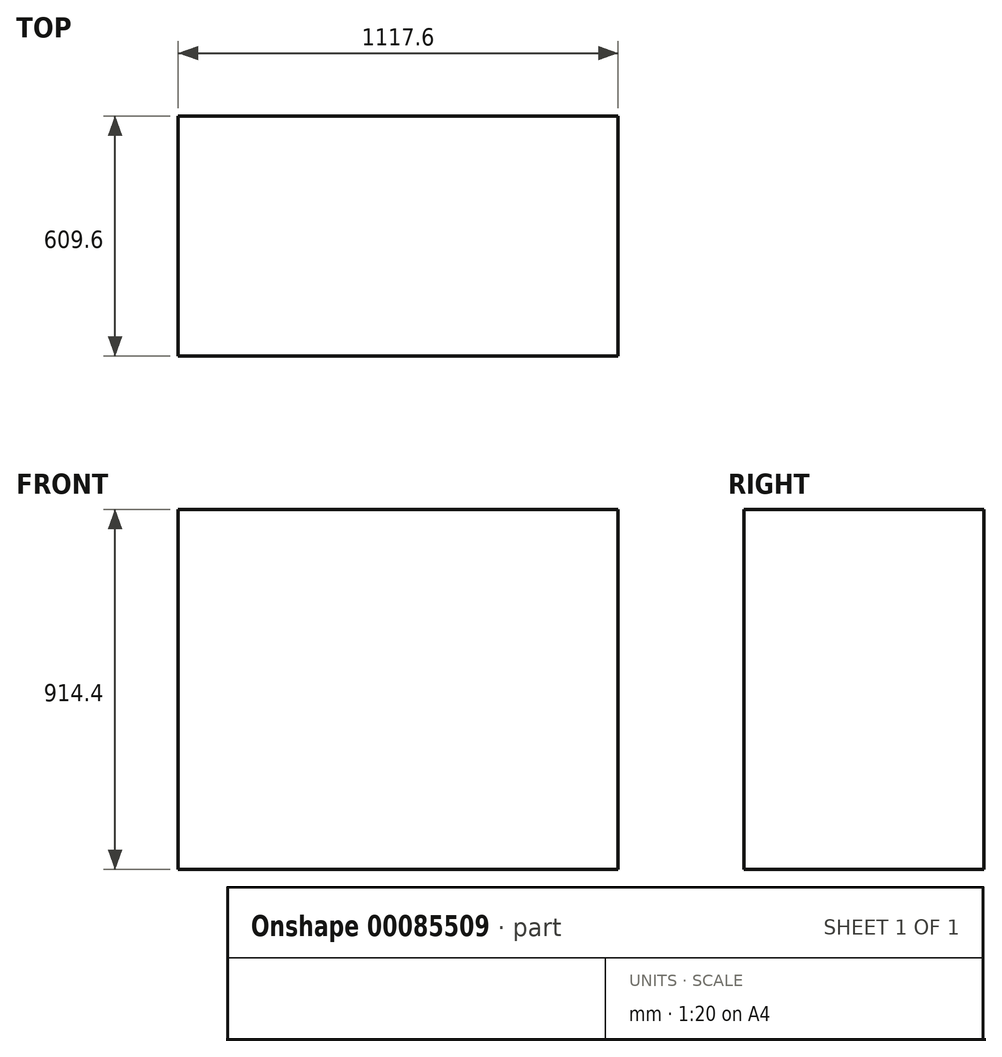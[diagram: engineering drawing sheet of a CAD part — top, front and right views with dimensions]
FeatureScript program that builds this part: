
annotation { "Feature Type Name" : "Feature", "Feature Type Description" : "" }
export const myFeature = defineFeature(function(context is Context, id is Id, definition is map)
    precondition{}
    {
        {
            var Q0;
            Q0=qCreatedBy(makeId("Top.planeOp"),FACE);
            var sketch = newSketch(context, id + "F0", { "sketchPlane" : qUnion([Q0])});
            skLineSegment(sketch, "E0.bottom", {"start": v(0, 0) * mm, "end": v(1117.6, 0) * mm});
            skLineSegment(sketch, "E0.top", {"start": v(0, 609.6) * mm, "end": v(1117.6, 609.6) * mm});
            skLineSegment(sketch, "E0.left", {"start": v(0, 0) * mm, "end": v(0, 609.6) * mm});
            skLineSegment(sketch, "E0.right", {"start": v(1117.6, 0) * mm, "end": v(1117.6, 609.6) * mm});
            skSolve(sketch);
        }
        {
            var Q0;
            Q0=makeQuery(id+"F0.imprint","IMPRINT",FACE,{"disambiguationData":[TD([[makeQuery(id+"F0.imprint","IMPRINT",EDGE,{"derivedFrom":sQuery(id+"F0.wireOp",EDGE,"E0.bottom")}),1.0]])]});
            extrude(context, id + "F1", {"entities" : qUnion([Q0]), "depth" : 914.4 * mm});
        }
    });
